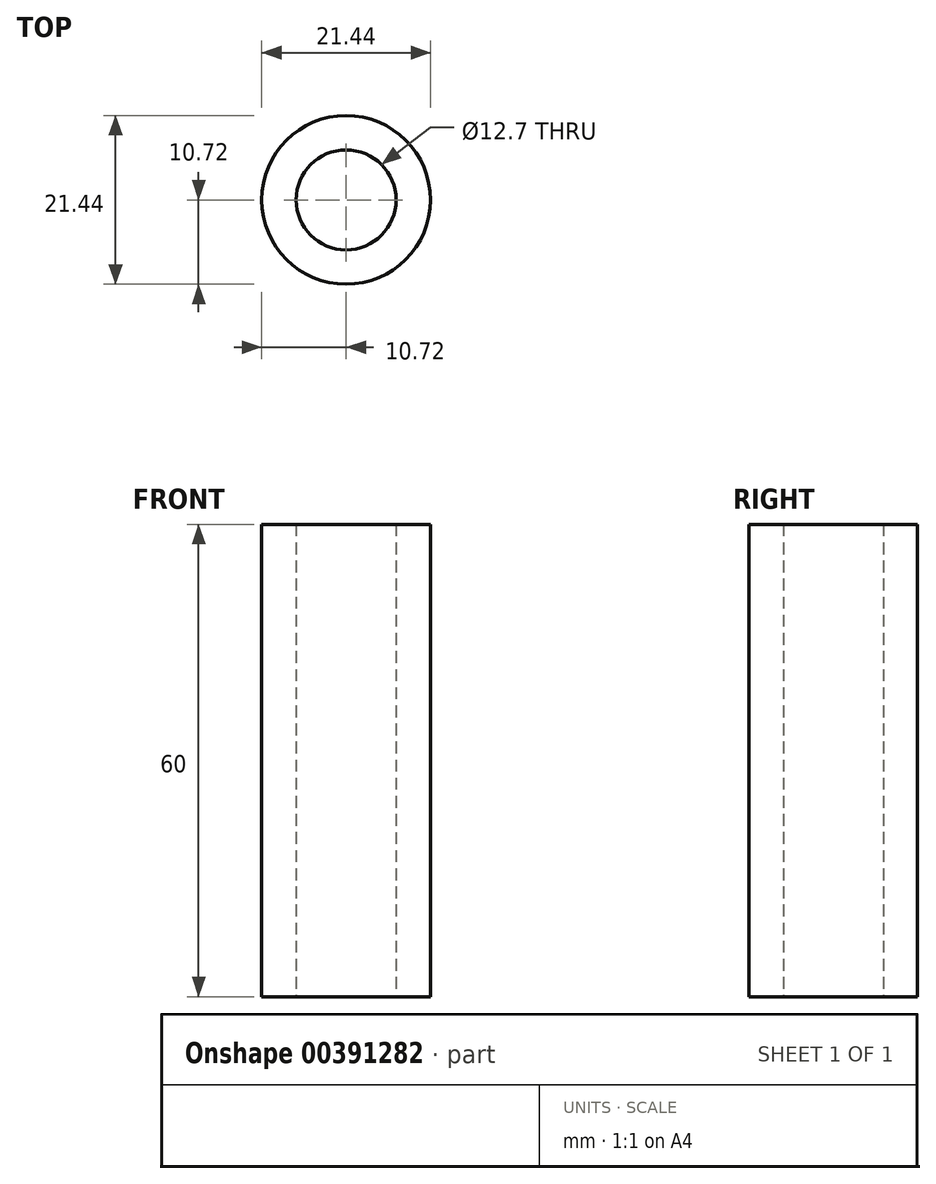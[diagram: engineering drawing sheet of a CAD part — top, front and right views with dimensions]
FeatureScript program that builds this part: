
annotation { "Feature Type Name" : "Feature", "Feature Type Description" : "" }
export const myFeature = defineFeature(function(context is Context, id is Id, definition is map)
    precondition{}
    {
        {
            assignVariable(context, id + "F0", {"name" : "Length", "anyValue" : 60});
        }
        {
            var Q0;
            Q0=qCreatedBy(makeId("Top.planeOp"),FACE);
            var sketch = newSketch(context, id + "F1", { "sketchPlane" : qUnion([Q0])});
            skCircle(sketch, "E0", {"center": v(0, 0) * mm, "radius": 10.72 * mm});
            skCircle(sketch, "E1", {"center": v(0, 0) * mm, "radius": 6.35 * mm});
            skSolve(sketch);
        }
        {
            var Q0;
            Q0=makeQuery(id+"F1.imprint","IMPRINT",FACE,{"disambiguationData":[TD([[makeQuery(id+"F1.imprint","IMPRINT",EDGE,{"derivedFrom":sQuery(id+"F1.wireOp",EDGE,"E0")}),1.0]])]});
            extrude(context, id + "F2", {"entities" : qUnion([Q0]), "depth" : (getVariable(context, 'Length')) * mm});
        }
    });
